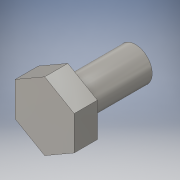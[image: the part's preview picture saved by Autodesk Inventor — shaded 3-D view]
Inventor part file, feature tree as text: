
AUTODESK INVENTOR PART (.ipt)
format: ipt  version: 2016 (Build 200138000, 138)  size: 117,248 bytes
history: native  units: in
note: dims shown in document units (in); Inventor stores cm internally (conversion verified against a paired STEP export)
features: other x13, extrude x2, sketch x2
ambient origin geometry x8: Origin, YZ Plane, XZ Plane, XY Plane, X Axis, Y Axis, Z Axis, Center Point
bodies: Solid1 (feature_tree)
feature tree (17):
  other  "Table"
  other  "bolt_hex_025-20-0500"
  other  "bolt_hex_025-20-0750"
  other  "bolt_hex_025-20-1000"
  other  "bolt_hex_025-20-1250"
  other  "bolt_hex_025-20-1500"
  other  "bolt_hex_025-20-1750"
  other  "bolt_hex_025-20-2000"
  other  "bolt_hex_025-20-2250"
  other  "bolt_hex_025-20-2500"
  other  "bolt_hex_025-20-3000"
  other  "bolt_hex_025-20-3500"
  other  "bolt_hex_025-20-4000"
  extrude  "Extrusion1"  TaperAngle=0.0deg  [1 undecoded]
  extrude  "Extrusion2"  [1 undecoded]
  sketch  "Sketch1"  dims[d2=0.0in d5=0.0in]
  sketch  "Sketch2"
note: 2 required parameter values undecoded (feature->parameter linkage not recoverable at this tier; creation-order binding heuristic only, values carry confidence <= 0.55)
